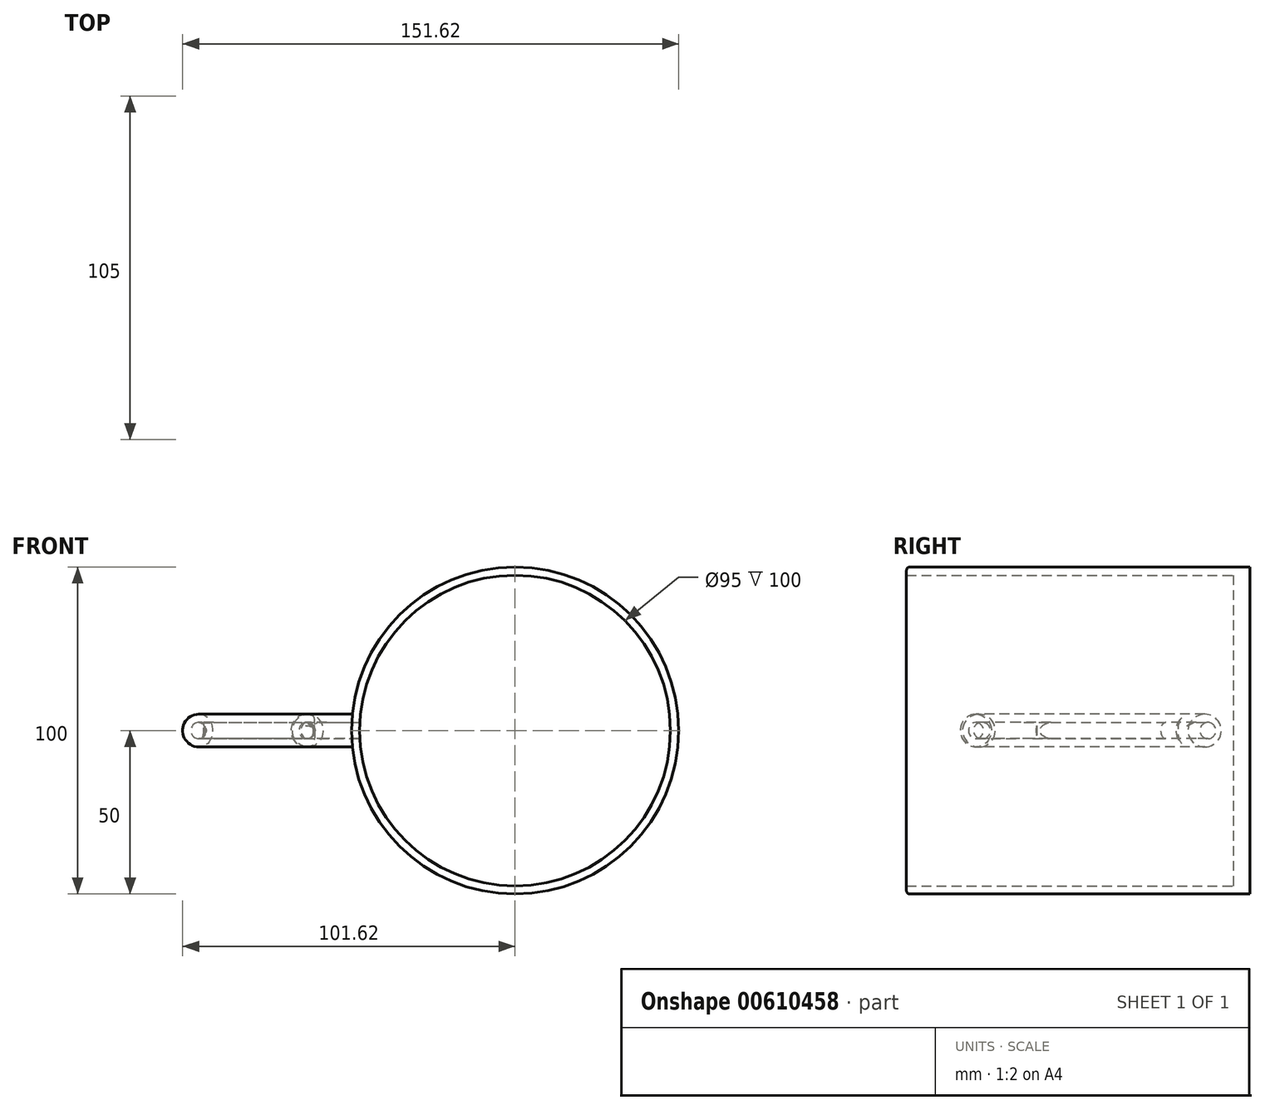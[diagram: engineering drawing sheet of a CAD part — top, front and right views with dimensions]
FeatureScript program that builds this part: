
annotation { "Feature Type Name" : "Feature", "Feature Type Description" : "" }
export const myFeature = defineFeature(function(context is Context, id is Id, definition is map)
    precondition{}
    {
        {
            var Q0;
            Q0=qCreatedBy(makeId("Front.planeOp"),FACE);
            var sketch = newSketch(context, id + "F0", { "sketchPlane" : qUnion([Q0])});
            skCircle(sketch, "E0", {"center": v(0, 0) * mm, "radius": 50 * mm});
            skSolve(sketch);
        }
        {
            var Q0;
            Q0=makeQuery(id+"F0.imprint","IMPRINT",FACE,{"disambiguationData":[TD([[makeQuery(id+"F0.imprint","IMPRINT",EDGE,{"derivedFrom":sQuery(id+"F0.wireOp",EDGE,"E0")}),1.0]])]});
            var Q1;
            Q1 = qSketchRegion(id + "F2", true);
            extrude(context, id + "F1", {"entities" : qUnion([Q0, Q1]), "depth" : 105 * mm, "offsetDistance" : 25 * mm});
        }
        {
            var Q0;
            Q0=qCreatedBy(makeId("Top.planeOp"),FACE);
            var sketch = newSketch(context, id + "F2", { "sketchPlane" : qUnion([Q0])});
            skFitSpline(sketch, "E1", {"points": [v(-49.05, -81.9) * mm, v(-86, -73.43) * mm, v(-95.67, -61.98) * mm, v(-64.78, -35.55) * mm, v(-62.93, -19.43) * mm, v(-58.87, -17.4) * mm, v(-46.18, -12.97) * mm], "startDerivative": vector(-131.4, -52.89) * mm, "endDerivative": vector(70.79, 30.94) * mm});
            skSolve(sketch);
        }
        {
            var Q0;
            Q0=qCreatedBy(makeId("Right.planeOp"),FACE);
            cPlane(context, id + "F3", {"entities" : qUnion([Q0]), "cplaneType" : CPlaneType.OFFSET, "offset" : 50 * mm, "oppositeDirection" : true, "width" : 150 * mm, "height" : 150 * mm});
        }
        {
            var Q0;
            Q0=qCreatedBy(id+"F3.planeOp",FACE);
            var sketch = newSketch(context, id + "F4", { "sketchPlane" : qUnion([Q0])});
            skCircle(sketch, "E2", {"center": v(-82.86, 0) * mm, "radius": 5 * mm});
            skSolve(sketch);
        }
        {
            var Q0;
            Q0=makeQuery(id+"F4.imprint","IMPRINT",FACE,{"disambiguationData":[TD([[makeQuery(id+"F4.imprint","IMPRINT",EDGE,{"derivedFrom":sQuery(id+"F4.wireOp",EDGE,"E2")}),1.0]])]});
            var Q1;
            Q1=sQuery(id+"F4.wireOp",EDGE,"E2");
            var Q2;
            Q2=sQuery(id+"F2.wireOp",EDGE,"E1");
            sweep(context, id + "F5", {"operationType" : NewBodyOperationType.ADD, "profiles" : qUnion([Q0]), "surfaceProfiles" : qUnion([Q1]), "path" : qUnion([Q2])});
        }
        {
            var Q0;
            Q0=makeQuery(id+"F1.opExtrude","CAP_EDGE",EDGE,{"disambiguationData":[OSD([sQuery(id+"F0.wireOp",EDGE,"E0")])],"isStart":false});
            fillet(context, id + "F6", {"entities" : qUnion([Q0]), "radius" : 1 * mm, "tangentPropagation" : true, "allowEdgeOverflow" : false});
        }
        {
            var Q0;
            Q0=makeQuery(id+"F1.opExtrude","CAP_FACE",FACE,{"disambiguationData":[OSD([sQuery(id+"F0.wireOp",EDGE,"E0")])],"isStart":false});
            shell(context, id + "F7", {"entities" : qUnion([Q0]), "thickness" : 2.5 * mm});
        }
        {
            var Q0;
            Q0=makeQuery(id+"F1.opExtrude","CAP_FACE",FACE,{"disambiguationData":[OSD([sQuery(id+"F0.wireOp",EDGE,"E0")])],"isStart":true});
            extrude(context, id + "F8", {"entities" : qUnion([Q0]), "operationType" : NewBodyOperationType.ADD, "oppositeDirection" : true, "depth" : 5 * mm, "offsetDistance" : 25 * mm});
        }
    });
